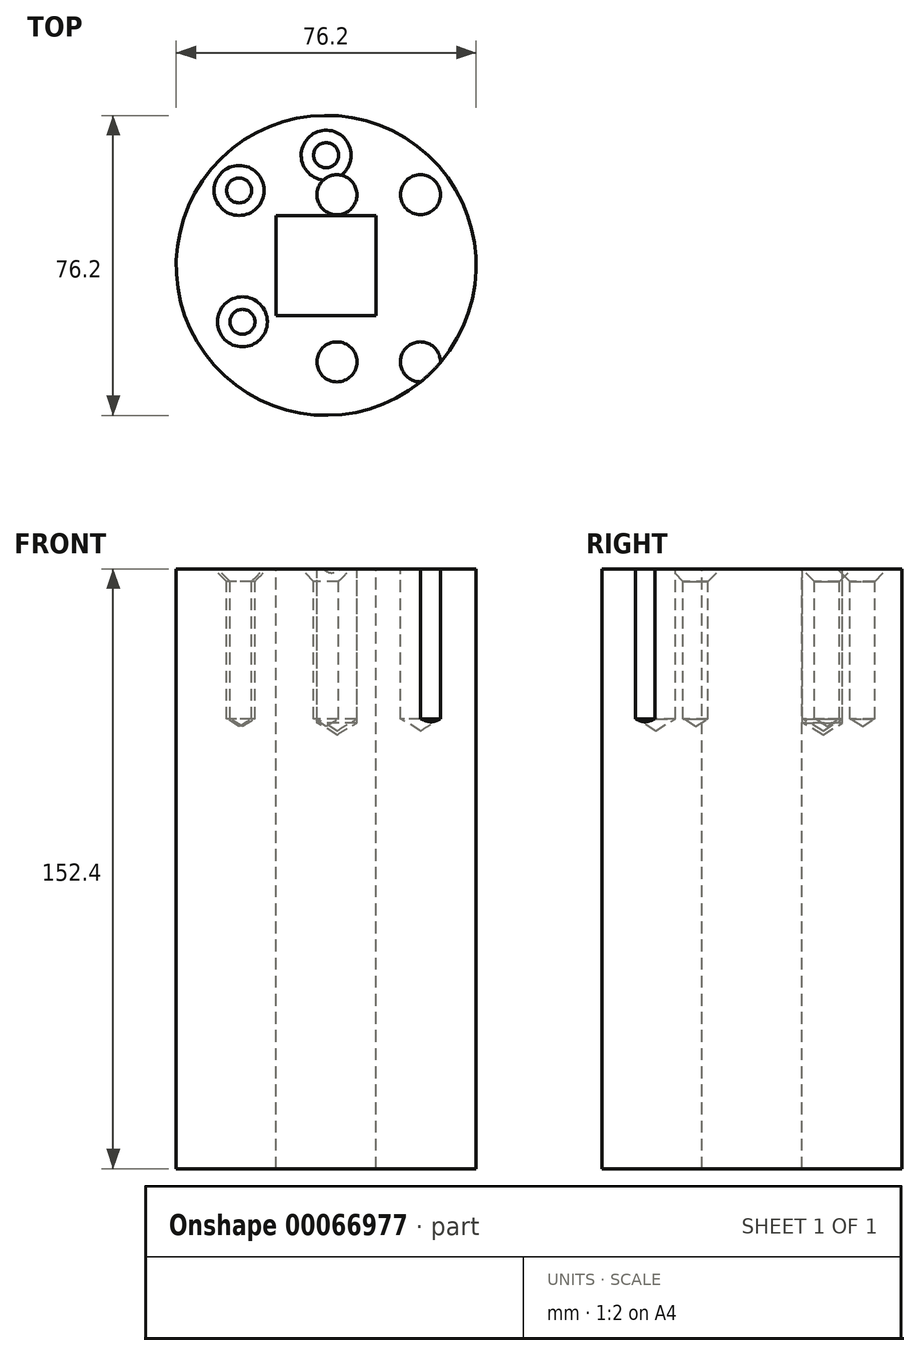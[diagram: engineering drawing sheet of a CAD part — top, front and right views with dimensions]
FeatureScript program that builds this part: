
annotation { "Feature Type Name" : "Feature", "Feature Type Description" : "" }
export const myFeature = defineFeature(function(context is Context, id is Id, definition is map)
    precondition{}
    {
        {
            var Q0;
            Q0=qCreatedBy(makeId("Top.planeOp"),FACE);
            var sketch = newSketch(context, id + "F0", { "sketchPlane" : qUnion([Q0])});
            skCircle(sketch, "E0", {"center": v(0, 0) * mm, "radius": 38.1 * mm});
            skSolve(sketch);
        }
        {
            var Q0;
            Q0 = qSketchRegion(id + "F0", true);
            extrude(context, id + "F1", {"entities" : qUnion([Q0]), "depth" : 152.4 * mm});
        }
        {
            var Q0;
            Q0=makeQuery(id+"F1.opExtrude","CAP_FACE",FACE,{"disambiguationData":[OSD([sQuery(id+"F0.wireOp",EDGE,"E0")])],"isStart":false});
            var sketch = newSketch(context, id + "F2", { "sketchPlane" : qUnion([Q0])});
            skLineSegment(sketch, "E1.bottom", {"start": v(-12.7, -12.7) * mm, "end": v(12.7, -12.7) * mm});
            skLineSegment(sketch, "E1.top", {"start": v(-12.7, 12.7) * mm, "end": v(12.7, 12.7) * mm});
            skLineSegment(sketch, "E1.left", {"start": v(-12.7, -12.7) * mm, "end": v(-12.7, 12.7) * mm});
            skLineSegment(sketch, "E1.right", {"start": v(12.7, -12.7) * mm, "end": v(12.7, 12.7) * mm});
            skLineSegment(sketch, "E2", {"start": v(-12.7, 12.7) * mm, "end": v(12.7, -12.7) * mm, "construction": true});
            skPoint(sketch, "E3", {"position": v(0, 0) * mm});
            skSolve(sketch);
        }
        {
            var Q0;
            Q0 = qSketchRegion(id + "F2", true);
            extrude(context, id + "F3", {"entities" : qUnion([Q0]), "operationType" : NewBodyOperationType.REMOVE, "endBound" : BoundingType.UP_TO_NEXT, "oppositeDirection" : true, "depth" : 25.4 * mm});
        }
        {
            var Q0;
            Q0=makeQuery(id+"F1.opExtrude","CAP_FACE",FACE,{"disambiguationData":[OSD([sQuery(id+"F0.wireOp",EDGE,"E0")])],"isStart":false});
            var sketch = newSketch(context, id + "F4", { "sketchPlane" : qUnion([Q0])});
            skPoint(sketch, "E4", {"position": v(-21.28, -14.34) * mm});
            skPoint(sketch, "E5", {"position": v(-22.11, 19.04) * mm});
            skPoint(sketch, "E6", {"position": v(0, 28) * mm});
            skSolve(sketch);
        }
        {
            var Q0;
            Q0=sQuery(id+"F4.wireOp",VERTEX,"E4");
            var Q1;
            Q1=sQuery(id+"F4.wireOp",VERTEX,"E5");
            var Q2;
            Q2=sQuery(id+"F4.wireOp",VERTEX,"E6");
            var Q3;
            Q3=makeQuery(id+"F1.opExtrude","SWEPT_BODY",BODY,{"disambiguationData":[OSD([sQuery(id+"F0.wireOp",EDGE,"E0")])]});
            hole(context, id + "F5", {"style" : HoleStyle.C_SINK, "holeDiameter" : 6.35 * mm, "cSinkDiameter" : 12.7 * mm, "endStyle" : HoleEndStyle.BLIND, "holeDepth" : 38.1 * mm, "locations" : qUnion([Q0, Q1, Q2]), "scope" : qUnion([Q3]), "cSinkAngle" : 90 * degree});
        }
        {
            var Q0;
            Q0=makeQuery(id+"F1.opExtrude","CAP_FACE",FACE,{"disambiguationData":[OSD([sQuery(id+"F0.wireOp",EDGE,"E0")])],"isStart":false});
            var sketch = newSketch(context, id + "F6", { "sketchPlane" : qUnion([Q0])});
            skLineSegment(sketch, "E7.bottom", {"start": v(2.74, -24.5) * mm, "end": v(23.96, -24.5) * mm});
            skLineSegment(sketch, "E7.top", {"start": v(2.74, 17.94) * mm, "end": v(23.96, 17.94) * mm});
            skLineSegment(sketch, "E7.left", {"start": v(2.74, -24.5) * mm, "end": v(2.74, 17.94) * mm});
            skLineSegment(sketch, "E7.right", {"start": v(23.96, -24.5) * mm, "end": v(23.96, 17.94) * mm});
            skSolve(sketch);
        }
        {
            var Q0;
            Q0=sQuery(id+"F6.wireOp",VERTEX,"E7.left.start");
            var Q1;
            Q1=sQuery(id+"F6.wireOp",VERTEX,"E7.right.start");
            var Q2;
            Q2=sQuery(id+"F6.wireOp",VERTEX,"E7.top.end");
            var Q3;
            Q3=sQuery(id+"F6.wireOp",VERTEX,"E7.left.end");
            var Q4;
            Q4=makeQuery(id+"F1.opExtrude","SWEPT_BODY",BODY,{"disambiguationData":[OSD([sQuery(id+"F0.wireOp",EDGE,"E0")])]});
            hole(context, id + "F7", {"style" : HoleStyle.SIMPLE, "holeDiameter" : 10.16 * mm, "endStyle" : HoleEndStyle.BLIND, "holeDepth" : 38.1 * mm, "locations" : qUnion([Q0, Q1, Q2, Q3]), "scope" : qUnion([Q4])});
        }
    });
